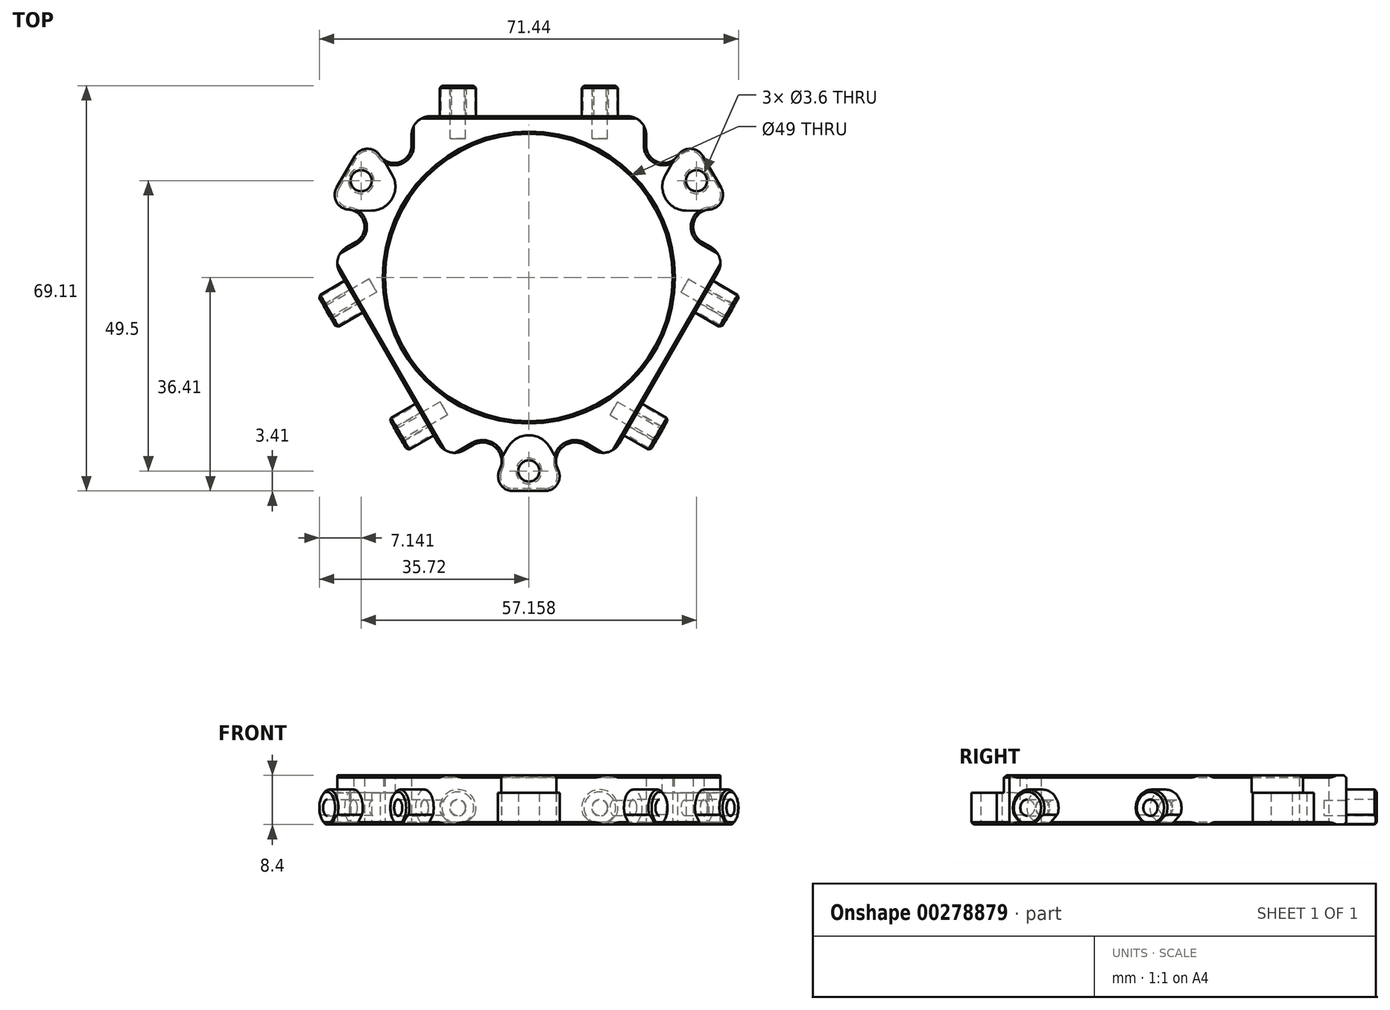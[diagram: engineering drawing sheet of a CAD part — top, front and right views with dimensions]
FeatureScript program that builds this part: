
annotation { "Feature Type Name" : "Feature", "Feature Type Description" : "" }
export const myFeature = defineFeature(function(context is Context, id is Id, definition is map)
    precondition{}
    {
        {
            var Q0;
            Q0=qCreatedBy(makeId("Top.planeOp"),FACE);
            var sketch = newSketch(context, id + "F0", { "sketchPlane" : qUnion([Q0])});
            skArc(sketch, "E0", {"start": v(3.94, -31.71) * mm, "mid": v(0, -27) * mm, "end": v(-3.94, -31.71) * mm});
            skArc(sketch, "E1", {"start": v(0.48, -34.97) * mm, "mid": v(4.46, -35.73) * mm, "end": v(3.94, -31.71) * mm});
            skLineSegment(sketch, "E2", {"start": v(3.73, -29.55) * mm, "end": v(5.07, -33) * mm});
            skCircle(sketch, "E3", {"center": v(0, 0) * mm, "radius": 24.5 * mm});
            skLineSegment(sketch, "E4", {"start": v(2.75, -36.4) * mm, "end": v(0, -36.4) * mm});
            skLineSegment(sketch, "E5.MirrorCS", {"start": v(-3.73, -29.55) * mm, "end": v(-5.07, -33) * mm});
            skArc(sketch, "E6.MirrorCS", {"start": v(-0.48, -34.97) * mm, "mid": v(-4.46, -35.73) * mm, "end": v(-3.94, -31.71) * mm});
            skLineSegment(sketch, "E7.MirrorCS", {"start": v(-2.75, -36.4) * mm, "end": v(0, -36.4) * mm});
            skLineSegment(sketch, "E8", {"start": v(0, 27.5) * mm, "end": v(12, 27.5) * mm});
            skLineSegment(sketch, "E9", {"start": v(12, 27.5) * mm, "end": v(20, 27.5) * mm});
            skLineSegment(sketch, "E10", {"start": v(20, 27.5) * mm, "end": v(20, 22.5) * mm});
            skLineSegment(sketch, "E11.MirrorCS", {"start": v(0, 27.5) * mm, "end": v(-12, 27.5) * mm});
            skLineSegment(sketch, "E12.MirrorCS", {"start": v(-12, 27.5) * mm, "end": v(-20, 27.5) * mm});
            skLineSegment(sketch, "E13.MirrorCS", {"start": v(-20, 27.5) * mm, "end": v(-20, 22.5) * mm});
            skLineSegment(sketch, "E14.1.0", {"start": v(-13.82, -31.07) * mm, "end": v(-9.49, -28.57) * mm});
            skLineSegment(sketch, "E14.1.1", {"start": v(-17.82, -24.14) * mm, "end": v(-13.82, -31.07) * mm});
            skLineSegment(sketch, "E14.1.2", {"start": v(-23.82, -13.75) * mm, "end": v(-17.82, -24.14) * mm});
            skLineSegment(sketch, "E14.1.3", {"start": v(-23.82, -13.75) * mm, "end": v(-29.82, -3.36) * mm});
            skLineSegment(sketch, "E14.1.4", {"start": v(-29.82, -3.36) * mm, "end": v(-33.82, 3.57) * mm});
            skLineSegment(sketch, "E14.1.5", {"start": v(-33.82, 3.57) * mm, "end": v(-29.49, 6.07) * mm});
            skLineSegment(sketch, "E14.2.0", {"start": v(33.82, 3.57) * mm, "end": v(29.49, 6.07) * mm});
            skLineSegment(sketch, "E14.2.1", {"start": v(29.82, -3.36) * mm, "end": v(33.82, 3.57) * mm});
            skLineSegment(sketch, "E14.2.2", {"start": v(23.82, -13.75) * mm, "end": v(29.82, -3.36) * mm});
            skLineSegment(sketch, "E14.2.3", {"start": v(23.82, -13.75) * mm, "end": v(17.82, -24.14) * mm});
            skLineSegment(sketch, "E14.2.4", {"start": v(17.82, -24.14) * mm, "end": v(13.82, -31.07) * mm});
            skLineSegment(sketch, "E14.2.5", {"start": v(13.82, -31.07) * mm, "end": v(9.49, -28.57) * mm});
            skArc(sketch, "E15", {"start": v(9.49, -28.57) * mm, "mid": v(5.58, -29.09) * mm, "end": v(5.07, -33) * mm});
            skArc(sketch, "E16.MirrorCS", {"start": v(-9.49, -28.57) * mm, "mid": v(-5.58, -29.09) * mm, "end": v(-5.07, -33) * mm});
            skArc(sketch, "E17.trimOffspring", {"start": v(-0.48, -34.97) * mm, "mid": v(0, -35) * mm, "end": v(0.48, -34.97) * mm});
            skArc(sketch, "E18.1.1", {"start": v(25.02, 19.06) * mm, "mid": v(23.38, 13.5) * mm, "end": v(29.01, 12.14) * mm});
            skArc(sketch, "E18.1.2", {"start": v(29.7, 18.3) * mm, "mid": v(27.9, 21.92) * mm, "end": v(25.02, 19.06) * mm});
            skArc(sketch, "E18.1.3", {"start": v(30.7, 16.58) * mm, "mid": v(32.92, 13.2) * mm, "end": v(29.01, 12.14) * mm});
            skArc(sketch, "E18.1.4", {"start": v(30.7, 16.58) * mm, "mid": v(30.31, 17.5) * mm, "end": v(29.7, 18.3) * mm});
            skLineSegment(sketch, "E18.1.5", {"start": v(26.94, 11.5) * mm, "end": v(30.64, 11.58) * mm});
            skLineSegment(sketch, "E18.1.6", {"start": v(23.43, 17.58) * mm, "end": v(25.35, 20.75) * mm});
            skLineSegment(sketch, "E18.1.7", {"start": v(29.65, 20.7) * mm, "end": v(31.2, 18.02) * mm});
            skLineSegment(sketch, "E18.1.8", {"start": v(32.75, 15.33) * mm, "end": v(31.2, 18.02) * mm});
            skArc(sketch, "E18.1.9", {"start": v(20, 22.5) * mm, "mid": v(22.04, 19.68) * mm, "end": v(25.35, 20.75) * mm});
            skArc(sketch, "E18.1.10", {"start": v(29.49, 6.07) * mm, "mid": v(28.07, 9.25) * mm, "end": v(30.64, 11.58) * mm});
            skArc(sketch, "E18.2.1", {"start": v(-29.01, 12.14) * mm, "mid": v(-23.38, 13.5) * mm, "end": v(-25.02, 19.06) * mm});
            skArc(sketch, "E18.2.2", {"start": v(-30.7, 16.58) * mm, "mid": v(-32.92, 13.2) * mm, "end": v(-29.01, 12.14) * mm});
            skArc(sketch, "E18.2.3", {"start": v(-29.7, 18.3) * mm, "mid": v(-27.9, 21.92) * mm, "end": v(-25.02, 19.06) * mm});
            skArc(sketch, "E18.2.4", {"start": v(-29.7, 18.3) * mm, "mid": v(-30.31, 17.5) * mm, "end": v(-30.7, 16.58) * mm});
            skLineSegment(sketch, "E18.2.5", {"start": v(-23.43, 17.58) * mm, "end": v(-25.35, 20.75) * mm});
            skLineSegment(sketch, "E18.2.6", {"start": v(-26.94, 11.5) * mm, "end": v(-30.64, 11.58) * mm});
            skLineSegment(sketch, "E18.2.7", {"start": v(-32.75, 15.33) * mm, "end": v(-31.2, 18.02) * mm});
            skLineSegment(sketch, "E18.2.8", {"start": v(-29.65, 20.7) * mm, "end": v(-31.2, 18.02) * mm});
            skArc(sketch, "E18.2.9", {"start": v(-29.49, 6.07) * mm, "mid": v(-28.07, 9.25) * mm, "end": v(-30.64, 11.58) * mm});
            skArc(sketch, "E18.2.10", {"start": v(-20, 22.5) * mm, "mid": v(-22.04, 19.68) * mm, "end": v(-25.35, 20.75) * mm});
            skCircle(sketch, "E19", {"center": v(0, -33) * mm, "radius": 1.8 * mm});
            skCircle(sketch, "E20.1.0", {"center": v(28.58, 16.5) * mm, "radius": 1.8 * mm});
            skCircle(sketch, "E20.2.0", {"center": v(-28.58, 16.5) * mm, "radius": 1.8 * mm});
            skSolve(sketch);
        }
        {
            var Q0;
            Q0=qSketchRegion(id+"F0",true);
            extrude(context, id + "F1", {"entities" : qUnion([Q0]), "depth" : 8.4 * mm, "offsetDistance" : 25 * mm});
        }
        {
            var Q0;
            Q0=makeQuery(id+"F1.opExtrude","SWEPT_FACE",FACE,{"disambiguationData":[OSD([sQuery(id+"F0.wireOp",EDGE,"E8"),sQuery(id+"F0.wireOp",EDGE,"E9"),sQuery(id+"F0.wireOp",EDGE,"E11.MirrorCS"),sQuery(id+"F0.wireOp",EDGE,"E12.MirrorCS")])]});
            var sketch = newSketch(context, id + "F2", { "sketchPlane" : qUnion([Q0])});
            skCircle(sketch, "E21.cCircle", {"center": v(-12.1, 2.86) * mm, "radius": 2.86 * mm, "construction": true});
            skLineSegment(sketch, "E21.0", {"start": v(-13.29, 5.73) * mm, "end": v(-10.91, 5.73) * mm});
            skLineSegment(sketch, "E21.1", {"start": v(-10.91, 5.73) * mm, "end": v(-9.24, 4.05) * mm});
            skLineSegment(sketch, "E21.2", {"start": v(-9.24, 4.05) * mm, "end": v(-9.24, 1.68) * mm});
            skLineSegment(sketch, "E21.3", {"start": v(-9.24, 1.68) * mm, "end": v(-10.91, 0) * mm});
            skLineSegment(sketch, "E21.4", {"start": v(-10.91, 0) * mm, "end": v(-13.29, 0) * mm});
            skLineSegment(sketch, "E21.5", {"start": v(-13.29, 0) * mm, "end": v(-14.96, 1.68) * mm});
            skLineSegment(sketch, "E21.6", {"start": v(-14.96, 1.68) * mm, "end": v(-14.96, 4.05) * mm});
            skLineSegment(sketch, "E21.7", {"start": v(-14.96, 4.05) * mm, "end": v(-13.29, 5.73) * mm});
            skPoint(sketch, "E21.0.midPoint", {"position": v(-12.1, 5.73) * mm});
            skArc(sketch, "E22", {"start": v(-9.24, 1.68) * mm, "mid": v(-12.1, 5.96) * mm, "end": v(-14.96, 1.68) * mm});
            skLineSegment(sketch, "E23.MirrorCS", {"start": v(10.91, 5.73) * mm, "end": v(9.24, 4.05) * mm});
            skLineSegment(sketch, "E24.MirrorCS", {"start": v(9.24, 4.05) * mm, "end": v(9.24, 1.68) * mm});
            skLineSegment(sketch, "E25.MirrorCS", {"start": v(14.96, 1.68) * mm, "end": v(14.96, 4.05) * mm});
            skLineSegment(sketch, "E26.MirrorCS", {"start": v(9.24, 1.68) * mm, "end": v(10.91, 0) * mm});
            skLineSegment(sketch, "E27.MirrorCS", {"start": v(14.96, 4.05) * mm, "end": v(13.29, 5.73) * mm});
            skLineSegment(sketch, "E28.MirrorCS", {"start": v(13.29, 5.73) * mm, "end": v(10.91, 5.73) * mm});
            skLineSegment(sketch, "E29.MirrorCS", {"start": v(10.91, 0) * mm, "end": v(13.29, 0) * mm});
            skLineSegment(sketch, "E30.MirrorCS", {"start": v(13.29, 0) * mm, "end": v(14.96, 1.68) * mm});
            skArc(sketch, "E31.MirrorCS", {"start": v(9.24, 1.68) * mm, "mid": v(12.1, 5.96) * mm, "end": v(14.96, 1.68) * mm});
            skPoint(sketch, "E32.MirrorP", {"position": v(12.1, 5.73) * mm});
            skCircle(sketch, "E33.MirrorC", {"center": v(12.1, 2.86) * mm, "radius": 2.86 * mm, "construction": true});
            skCircle(sketch, "E34", {"center": v(-12.1, 2.86) * mm, "radius": 1.4 * mm});
            skCircle(sketch, "E35.MirrorC", {"center": v(12.1, 2.86) * mm, "radius": 1.4 * mm});
            skSolve(sketch);
        }
        {
            var Q0;
            Q0=qSketchRegion(id+"F2",true);
            extrude(context, id + "F3", {"entities" : qUnion([Q0]), "depth" : 5.2 * mm, "offsetDistance" : 25 * mm});
        }
        {
            var Q0;
            Q0=makeQuery(id+"F3.opExtrude","CAP_FACE",FACE,{"disambiguationData":[OSD([sQuery(id+"F2.wireOp",EDGE,"E21.3"),sQuery(id+"F2.wireOp",EDGE,"E21.4"),sQuery(id+"F2.wireOp",EDGE,"E21.5"),sQuery(id+"F2.wireOp",EDGE,"E22"),sQuery(id+"F2.wireOp",EDGE,"E34")])],"isStart":false});
            var sketch = newSketch(context, id + "F4", { "sketchPlane" : qUnion([Q0])});
            skSolve(sketch);
        }
        {
            var Q0;
            Q0=makeQuery(id+"F3.opExtrude","SWEPT_BODY",BODY,{"disambiguationData":[OSD([sQuery(id+"F2.wireOp",EDGE,"E21.0"),sQuery(id+"F2.wireOp",EDGE,"E21.1"),sQuery(id+"F2.wireOp",EDGE,"E21.2"),sQuery(id+"F2.wireOp",EDGE,"E21.3"),sQuery(id+"F2.wireOp",EDGE,"E21.4"),sQuery(id+"F2.wireOp",EDGE,"E21.5"),sQuery(id+"F2.wireOp",EDGE,"E21.6"),sQuery(id+"F2.wireOp",EDGE,"E21.7")])]});
            var Q1;
            Q1=makeQuery(id+"F3.opExtrude","SWEPT_BODY",BODY,{"disambiguationData":[OSD([sQuery(id+"F2.wireOp",EDGE,"E26.MirrorCS"),sQuery(id+"F2.wireOp",EDGE,"E29.MirrorCS"),sQuery(id+"F2.wireOp",EDGE,"E30.MirrorCS"),sQuery(id+"F2.wireOp",EDGE,"E31.MirrorCS")])]});
            var Q2;
            Q2=makeQuery(id+"F1.opExtrude","CAP_EDGE",EDGE,{"disambiguationData":[OSD([sQuery(id+"F0.wireOp",EDGE,"E3")])],"isStart":false});
            circularPattern(context, id + "F5", {"operationType" : NewBodyOperationType.ADD, "entities" : qUnion([Q0, Q1]), "axis" : qUnion([Q2]), "angle" : 360 * degree, "instanceCount" : 3, "equalSpace" : true});
        }
        {
            var Q0;
            Q0=makeQuery(id+"F3.opExtrude","CAP_FACE",FACE,{"disambiguationData":[OSD([sQuery(id+"F2.wireOp",EDGE,"E21.3"),sQuery(id+"F2.wireOp",EDGE,"E21.4"),sQuery(id+"F2.wireOp",EDGE,"E21.5"),sQuery(id+"F2.wireOp",EDGE,"E22")])],"isStart":false});
            var sketch = newSketch(context, id + "F6", { "sketchPlane" : qUnion([Q0])});
            skCircle(sketch, "E36", {"center": v(-12.1, 2.86) * mm, "radius": 1.3 * mm});
            skCircle(sketch, "E37.MirrorC", {"center": v(12.1, 2.86) * mm, "radius": 1.3 * mm});
            skSolve(sketch);
        }
        {
            var Q0;
            Q0=qSketchRegion(id+"F6",true);
            extrude(context, id + "F7", {"entities" : qUnion([Q0]), "oppositeDirection" : true, "depth" : 9 * mm, "offsetDistance" : 25 * mm});
        }
        {
            var Q0;
            Q0=makeQuery(id+"F7.opExtrude","SWEPT_BODY",BODY,{"disambiguationData":[OSD([sQuery(id+"F6.wireOp",EDGE,"E37.MirrorC")])]});
            var Q1;
            Q1=makeQuery(id+"F7.opExtrude","SWEPT_BODY",BODY,{"disambiguationData":[OSD([sQuery(id+"F6.wireOp",EDGE,"E36")])]});
            var Q2;
            Q2=makeQuery(id+"F1.opExtrude","CAP_EDGE",EDGE,{"disambiguationData":[OSD([sQuery(id+"F0.wireOp",EDGE,"E3")])],"isStart":false});
            circularPattern(context, id + "F8", {"operationType" : NewBodyOperationType.REMOVE, "entities" : qUnion([Q0, Q1]), "axis" : qUnion([Q2]), "angle" : 360 * degree, "instanceCount" : 3, "equalSpace" : true});
        }
        {
            var Q0;
            {var subQ0=makeQuery(id+"F3.opExtrude","SWEPT_FACE",FACE,{"disambiguationData":[OSD([sQuery(id+"F2.wireOp",EDGE,"E29.MirrorCS")])]});var subQ1=makeQuery(id+"F3.opExtrude","SWEPT_FACE",FACE,{"disambiguationData":[OSD([sQuery(id+"F2.wireOp",EDGE,"E21.4")])]});Q0=makeQuery(id+"F5.boolean.opBoolean","MERGE",FACE,{"derivedFrom":[makeQuery(id+"F1.opExtrude","CAP_FACE",FACE,{"disambiguationData":[OSD([sQuery(id+"F0.wireOp",EDGE,"SqP7JoLz-BD9A-RXmz-Zu1V-RbqKSFD4Gl63"),sQuery(id+"F0.wireOp",EDGE,"Ud9Chbpr-zYe2-2spb-ifSY-rzAQWNdjOQxf"),sQuery(id+"F0.wireOp",EDGE,"bF6wv58Z-VzMq-CWjE-Sgwb-4WXWosELiao8"),sQuery(id+"F0.wireOp",EDGE,"cTkBJLnt-Smek-8MJw-4hbo-giizK2urv45t"),sQuery(id+"F0.wireOp",EDGE,"ae239fa6-1cef-4aa7-9151-0311c269b8940.MirrorCS"),sQuery(id+"F0.wireOp",EDGE,"ae239fa6-1cef-4aa7-9151-0311c269b8941.MirrorCS"),sQuery(id+"F0.wireOp",EDGE,"ae239fa6-1cef-4aa7-9151-0311c269b8943.MirrorCS"),sQuery(id+"F0.wireOp",EDGE,"ae239fa6-1cef-4aa7-9151-0311c269b8946.MirrorCS"),sQuery(id+"F0.wireOp",EDGE,"02da523c-332d-451a-b30c-e25d5381daab.1.0"),sQuery(id+"F0.wireOp",EDGE,"02da523c-332d-451a-b30c-e25d5381daab.1.1"),sQuery(id+"F0.wireOp",EDGE,"02da523c-332d-451a-b30c-e25d5381daab.1.2"),sQuery(id+"F0.wireOp",EDGE,"02da523c-332d-451a-b30c-e25d5381daab.1.5"),sQuery(id+"F0.wireOp",EDGE,"02da523c-332d-451a-b30c-e25d5381daab.1.6"),sQuery(id+"F0.wireOp",EDGE,"02da523c-332d-451a-b30c-e25d5381daab.1.8"),sQuery(id+"F0.wireOp",EDGE,"02da523c-332d-451a-b30c-e25d5381daab.1.9"),sQuery(id+"F0.wireOp",EDGE,"02da523c-332d-451a-b30c-e25d5381daab.1.15"),sQuery(id+"F0.wireOp",EDGE,"02da523c-332d-451a-b30c-e25d5381daab.1.16"),sQuery(id+"F0.wireOp",EDGE,"02da523c-332d-451a-b30c-e25d5381daab.2.0"),sQuery(id+"F0.wireOp",EDGE,"02da523c-332d-451a-b30c-e25d5381daab.2.1"),sQuery(id+"F0.wireOp",EDGE,"02da523c-332d-451a-b30c-e25d5381daab.2.2"),sQuery(id+"F0.wireOp",EDGE,"02da523c-332d-451a-b30c-e25d5381daab.2.5"),sQuery(id+"F0.wireOp",EDGE,"02da523c-332d-451a-b30c-e25d5381daab.2.6"),sQuery(id+"F0.wireOp",EDGE,"02da523c-332d-451a-b30c-e25d5381daab.2.8"),sQuery(id+"F0.wireOp",EDGE,"02da523c-332d-451a-b30c-e25d5381daab.2.9"),sQuery(id+"F0.wireOp",EDGE,"02da523c-332d-451a-b30c-e25d5381daab.2.11"),sQuery(id+"F0.wireOp",EDGE,"02da523c-332d-451a-b30c-e25d5381daab.2.15"),sQuery(id+"F0.wireOp",EDGE,"02da523c-332d-451a-b30c-e25d5381daab.2.16"),sQuery(id+"F0.wireOp",EDGE,"tuegAIGZ-9Pk6-ZTlW-QU7Y-IGKE2iZstJ9h"),sQuery(id+"F0.wireOp",EDGE,"fd02a02f-7cdf-416c-a631-e7393bf9c9300.MirrorC"),sQuery(id+"F0.wireOp",EDGE,"b5a6a487-fcb2-4526-9c33-14607ead2c7a.1.0"),sQuery(id+"F0.wireOp",EDGE,"b5a6a487-fcb2-4526-9c33-14607ead2c7a.1.1"),sQuery(id+"F0.wireOp",EDGE,"b5a6a487-fcb2-4526-9c33-14607ead2c7a.2.0"),sQuery(id+"F0.wireOp",EDGE,"b5a6a487-fcb2-4526-9c33-14607ead2c7a.2.1")])],"isStart":true}),subQ1,subQ0,makeQuery(id+"F5.opPattern","COPY",FACE,{"derivedFrom":subQ1,"instanceName":"1"}),makeQuery(id+"F5.opPattern","COPY",FACE,{"derivedFrom":subQ0,"instanceName":"1"}),makeQuery(id+"F5.opPattern","COPY",FACE,{"derivedFrom":subQ1,"instanceName":"2"}),makeQuery(id+"F5.opPattern","COPY",FACE,{"derivedFrom":subQ0,"instanceName":"2"})]});}
            var Q1;
            Q1=makeQuery(id+"F3.opExtrude","CAP_EDGE",EDGE,{"disambiguationData":[OSD([sQuery(id+"F2.wireOp",EDGE,"E31.MirrorCS")])],"isStart":false});
            var Q2;
            Q2=makeQuery(id+"F3.opExtrude","CAP_EDGE",EDGE,{"disambiguationData":[OSD([sQuery(id+"F2.wireOp",EDGE,"E22")])],"isStart":false});
            var Q3;
            Q3=makeQuery(id+"F5.opPattern","COPY",EDGE,{"derivedFrom":makeQuery(id+"F3.opExtrude","CAP_EDGE",EDGE,{"disambiguationData":[OSD([sQuery(id+"F2.wireOp",EDGE,"E31.MirrorCS")])],"isStart":false}),"instanceName":"2"});
            var Q4;
            Q4=makeQuery(id+"F5.opPattern","COPY",EDGE,{"derivedFrom":makeQuery(id+"F3.opExtrude","CAP_EDGE",EDGE,{"disambiguationData":[OSD([sQuery(id+"F2.wireOp",EDGE,"E22")])],"isStart":false}),"instanceName":"2"});
            var Q5;
            Q5=makeQuery(id+"F5.opPattern","COPY",EDGE,{"derivedFrom":makeQuery(id+"F3.opExtrude","CAP_EDGE",EDGE,{"disambiguationData":[OSD([sQuery(id+"F2.wireOp",EDGE,"E31.MirrorCS")])],"isStart":false}),"instanceName":"1"});
            var Q6;
            Q6=makeQuery(id+"F5.opPattern","COPY",EDGE,{"derivedFrom":makeQuery(id+"F3.opExtrude","CAP_EDGE",EDGE,{"disambiguationData":[OSD([sQuery(id+"F2.wireOp",EDGE,"E22")])],"isStart":false}),"instanceName":"1"});
            var Q7;
            Q7=makeQuery(id+"F1.opExtrude","CAP_FACE",FACE,{"disambiguationData":[OSD([sQuery(id+"F0.wireOp",EDGE,"SqP7JoLz-BD9A-RXmz-Zu1V-RbqKSFD4Gl63"),sQuery(id+"F0.wireOp",EDGE,"Ud9Chbpr-zYe2-2spb-ifSY-rzAQWNdjOQxf"),sQuery(id+"F0.wireOp",EDGE,"bF6wv58Z-VzMq-CWjE-Sgwb-4WXWosELiao8"),sQuery(id+"F0.wireOp",EDGE,"cTkBJLnt-Smek-8MJw-4hbo-giizK2urv45t"),sQuery(id+"F0.wireOp",EDGE,"ae239fa6-1cef-4aa7-9151-0311c269b8940.MirrorCS"),sQuery(id+"F0.wireOp",EDGE,"ae239fa6-1cef-4aa7-9151-0311c269b8941.MirrorCS"),sQuery(id+"F0.wireOp",EDGE,"ae239fa6-1cef-4aa7-9151-0311c269b8943.MirrorCS"),sQuery(id+"F0.wireOp",EDGE,"ae239fa6-1cef-4aa7-9151-0311c269b8946.MirrorCS"),sQuery(id+"F0.wireOp",EDGE,"02da523c-332d-451a-b30c-e25d5381daab.1.0"),sQuery(id+"F0.wireOp",EDGE,"02da523c-332d-451a-b30c-e25d5381daab.1.1"),sQuery(id+"F0.wireOp",EDGE,"02da523c-332d-451a-b30c-e25d5381daab.1.2"),sQuery(id+"F0.wireOp",EDGE,"02da523c-332d-451a-b30c-e25d5381daab.1.5"),sQuery(id+"F0.wireOp",EDGE,"02da523c-332d-451a-b30c-e25d5381daab.1.6"),sQuery(id+"F0.wireOp",EDGE,"02da523c-332d-451a-b30c-e25d5381daab.1.8"),sQuery(id+"F0.wireOp",EDGE,"02da523c-332d-451a-b30c-e25d5381daab.1.9"),sQuery(id+"F0.wireOp",EDGE,"02da523c-332d-451a-b30c-e25d5381daab.1.15"),sQuery(id+"F0.wireOp",EDGE,"02da523c-332d-451a-b30c-e25d5381daab.1.16"),sQuery(id+"F0.wireOp",EDGE,"02da523c-332d-451a-b30c-e25d5381daab.2.0"),sQuery(id+"F0.wireOp",EDGE,"02da523c-332d-451a-b30c-e25d5381daab.2.1"),sQuery(id+"F0.wireOp",EDGE,"02da523c-332d-451a-b30c-e25d5381daab.2.2"),sQuery(id+"F0.wireOp",EDGE,"02da523c-332d-451a-b30c-e25d5381daab.2.5"),sQuery(id+"F0.wireOp",EDGE,"02da523c-332d-451a-b30c-e25d5381daab.2.6"),sQuery(id+"F0.wireOp",EDGE,"02da523c-332d-451a-b30c-e25d5381daab.2.8"),sQuery(id+"F0.wireOp",EDGE,"02da523c-332d-451a-b30c-e25d5381daab.2.9"),sQuery(id+"F0.wireOp",EDGE,"02da523c-332d-451a-b30c-e25d5381daab.2.11"),sQuery(id+"F0.wireOp",EDGE,"02da523c-332d-451a-b30c-e25d5381daab.2.15"),sQuery(id+"F0.wireOp",EDGE,"02da523c-332d-451a-b30c-e25d5381daab.2.16"),sQuery(id+"F0.wireOp",EDGE,"tuegAIGZ-9Pk6-ZTlW-QU7Y-IGKE2iZstJ9h"),sQuery(id+"F0.wireOp",EDGE,"fd02a02f-7cdf-416c-a631-e7393bf9c9300.MirrorC"),sQuery(id+"F0.wireOp",EDGE,"b5a6a487-fcb2-4526-9c33-14607ead2c7a.1.0"),sQuery(id+"F0.wireOp",EDGE,"b5a6a487-fcb2-4526-9c33-14607ead2c7a.1.1"),sQuery(id+"F0.wireOp",EDGE,"b5a6a487-fcb2-4526-9c33-14607ead2c7a.2.0"),sQuery(id+"F0.wireOp",EDGE,"b5a6a487-fcb2-4526-9c33-14607ead2c7a.2.1")])],"isStart":false});
            var Q8;
            Q8=makeQuery(id+"F1.opExtrude","CAP_FACE",FACE,{"disambiguationData":[OSD([sQuery(id+"F0.wireOp",EDGE,"E1"),sQuery(id+"F0.wireOp",EDGE,"E3"),sQuery(id+"F0.wireOp",EDGE,"E4"),sQuery(id+"F0.wireOp",EDGE,"E6.MirrorCS"),sQuery(id+"F0.wireOp",EDGE,"E7.MirrorCS"),sQuery(id+"F0.wireOp",EDGE,"NR2aZ9zS-O8kZ-dOxt-Ha0G-w07LVY2dGel9"),sQuery(id+"F0.wireOp",EDGE,"E8"),sQuery(id+"F0.wireOp",EDGE,"E9"),sQuery(id+"F0.wireOp",EDGE,"E10"),sQuery(id+"F0.wireOp",EDGE,"E11.MirrorCS"),sQuery(id+"F0.wireOp",EDGE,"E12.MirrorCS"),sQuery(id+"F0.wireOp",EDGE,"E13.MirrorCS"),sQuery(id+"F0.wireOp",EDGE,"E14.1.0"),sQuery(id+"F0.wireOp",EDGE,"E14.1.1"),sQuery(id+"F0.wireOp",EDGE,"E14.1.2"),sQuery(id+"F0.wireOp",EDGE,"E14.1.3"),sQuery(id+"F0.wireOp",EDGE,"E14.1.4"),sQuery(id+"F0.wireOp",EDGE,"E14.1.5"),sQuery(id+"F0.wireOp",EDGE,"E14.2.0"),sQuery(id+"F0.wireOp",EDGE,"E14.2.1"),sQuery(id+"F0.wireOp",EDGE,"E14.2.2"),sQuery(id+"F0.wireOp",EDGE,"E14.2.3"),sQuery(id+"F0.wireOp",EDGE,"E14.2.4"),sQuery(id+"F0.wireOp",EDGE,"E14.2.5"),sQuery(id+"F0.wireOp",EDGE,"E15"),sQuery(id+"F0.wireOp",EDGE,"E16.MirrorCS"),sQuery(id+"F0.wireOp",EDGE,"E18.1.0"),sQuery(id+"F0.wireOp",EDGE,"E18.1.2"),sQuery(id+"F0.wireOp",EDGE,"E18.1.3"),sQuery(id+"F0.wireOp",EDGE,"E18.1.7"),sQuery(id+"F0.wireOp",EDGE,"E18.1.8"),sQuery(id+"F0.wireOp",EDGE,"E18.1.9"),sQuery(id+"F0.wireOp",EDGE,"E18.1.10"),sQuery(id+"F0.wireOp",EDGE,"E18.2.0"),sQuery(id+"F0.wireOp",EDGE,"E18.2.2"),sQuery(id+"F0.wireOp",EDGE,"E18.2.3"),sQuery(id+"F0.wireOp",EDGE,"E18.2.7"),sQuery(id+"F0.wireOp",EDGE,"E18.2.8"),sQuery(id+"F0.wireOp",EDGE,"E18.2.9"),sQuery(id+"F0.wireOp",EDGE,"E18.2.10")])],"isStart":false});
            chamfer(context, id + "F9", {"entities" : qUnion([Q0, Q1, Q2, Q3, Q4, Q5, Q6, Q7, Q8]), "width" : .4 * mm, "tangentPropagation" : true});
        }
        {
            var Q0;
            Q0=makeQuery(id+"F1.opExtrude","SWEPT_EDGE",EDGE,{"disambiguationData":[OSD([sQuery(id+"F0.wireOp",EDGE,"E14.1.4"),sQuery(id+"F0.wireOp",EDGE,"E14.1.5")])]});
            var Q1;
            Q1=makeQuery(id+"F1.opExtrude","SWEPT_EDGE",EDGE,{"disambiguationData":[OSD([sQuery(id+"F0.wireOp",EDGE,"E14.1.0"),sQuery(id+"F0.wireOp",EDGE,"E14.1.1")])]});
            var Q2;
            Q2=makeQuery(id+"F1.opExtrude","SWEPT_EDGE",EDGE,{"disambiguationData":[OSD([sQuery(id+"F0.wireOp",EDGE,"E14.2.4"),sQuery(id+"F0.wireOp",EDGE,"E14.2.5")])]});
            var Q3;
            Q3=makeQuery(id+"F1.opExtrude","SWEPT_EDGE",EDGE,{"disambiguationData":[OSD([sQuery(id+"F0.wireOp",EDGE,"E14.2.0"),sQuery(id+"F0.wireOp",EDGE,"E14.2.1")])]});
            var Q4;
            Q4=makeQuery(id+"F1.opExtrude","SWEPT_EDGE",EDGE,{"disambiguationData":[OSD([sQuery(id+"F0.wireOp",EDGE,"E9"),sQuery(id+"F0.wireOp",EDGE,"E10")])]});
            var Q5;
            Q5=makeQuery(id+"F1.opExtrude","SWEPT_EDGE",EDGE,{"disambiguationData":[OSD([sQuery(id+"F0.wireOp",EDGE,"E12.MirrorCS"),sQuery(id+"F0.wireOp",EDGE,"E13.MirrorCS")])]});
            fillet(context, id + "F10", {"entities" : qUnion([Q0, Q1, Q2, Q3, Q4, Q5]), "radius" : 3.2 * mm, "tangentPropagation" : true, "allowEdgeOverflow" : false});
        }
        {
            var Q0;
            Q0=makeQuery(id+"F1.opExtrude","CAP_FACE",FACE,{"disambiguationData":[OSD([sQuery(id+"F0.wireOp",EDGE,"E1"),sQuery(id+"F0.wireOp",EDGE,"E3"),sQuery(id+"F0.wireOp",EDGE,"E4"),sQuery(id+"F0.wireOp",EDGE,"E6.MirrorCS"),sQuery(id+"F0.wireOp",EDGE,"E7.MirrorCS"),sQuery(id+"F0.wireOp",EDGE,"NR2aZ9zS-O8kZ-dOxt-Ha0G-w07LVY2dGel9"),sQuery(id+"F0.wireOp",EDGE,"E8"),sQuery(id+"F0.wireOp",EDGE,"E9"),sQuery(id+"F0.wireOp",EDGE,"E10"),sQuery(id+"F0.wireOp",EDGE,"E11.MirrorCS"),sQuery(id+"F0.wireOp",EDGE,"E12.MirrorCS"),sQuery(id+"F0.wireOp",EDGE,"E13.MirrorCS"),sQuery(id+"F0.wireOp",EDGE,"E14.1.0"),sQuery(id+"F0.wireOp",EDGE,"E14.1.1"),sQuery(id+"F0.wireOp",EDGE,"E14.1.2"),sQuery(id+"F0.wireOp",EDGE,"E14.1.3"),sQuery(id+"F0.wireOp",EDGE,"E14.1.4"),sQuery(id+"F0.wireOp",EDGE,"E14.1.5"),sQuery(id+"F0.wireOp",EDGE,"E14.2.0"),sQuery(id+"F0.wireOp",EDGE,"E14.2.1"),sQuery(id+"F0.wireOp",EDGE,"E14.2.2"),sQuery(id+"F0.wireOp",EDGE,"E14.2.3"),sQuery(id+"F0.wireOp",EDGE,"E14.2.4"),sQuery(id+"F0.wireOp",EDGE,"E14.2.5"),sQuery(id+"F0.wireOp",EDGE,"E15"),sQuery(id+"F0.wireOp",EDGE,"E16.MirrorCS"),sQuery(id+"F0.wireOp",EDGE,"E18.1.0"),sQuery(id+"F0.wireOp",EDGE,"E18.1.2"),sQuery(id+"F0.wireOp",EDGE,"E18.1.3"),sQuery(id+"F0.wireOp",EDGE,"E18.1.7"),sQuery(id+"F0.wireOp",EDGE,"E18.1.8"),sQuery(id+"F0.wireOp",EDGE,"E18.1.9"),sQuery(id+"F0.wireOp",EDGE,"E18.1.10"),sQuery(id+"F0.wireOp",EDGE,"E18.2.0"),sQuery(id+"F0.wireOp",EDGE,"E18.2.2"),sQuery(id+"F0.wireOp",EDGE,"E18.2.3"),sQuery(id+"F0.wireOp",EDGE,"E18.2.7"),sQuery(id+"F0.wireOp",EDGE,"E18.2.8"),sQuery(id+"F0.wireOp",EDGE,"E18.2.9"),sQuery(id+"F0.wireOp",EDGE,"E18.2.10")])],"isStart":false});
            var sketch = newSketch(context, id + "F11", { "sketchPlane" : qUnion([Q0])});
            skArc(sketch, "E38", {"start": v(4.1, -31.08) * mm, "mid": v(0, -26.9) * mm, "end": v(-4.1, -31.08) * mm});
            skArc(sketch, "E39", {"start": v(0.22, -35.1) * mm, "mid": v(5.1, -35.94) * mm, "end": v(4.1, -31.08) * mm});
            skLineSegment(sketch, "E40", {"start": v(3.54, -28.93) * mm, "end": v(5.53, -32.33) * mm});
            skLineSegment(sketch, "E41", {"start": v(2.95, -36.85) * mm, "end": v(0, -36.85) * mm});
            skLineSegment(sketch, "E42.MirrorCS", {"start": v(-3.54, -28.93) * mm, "end": v(-5.53, -32.33) * mm});
            skArc(sketch, "E43.MirrorCS", {"start": v(-0.22, -35.1) * mm, "mid": v(-5.1, -35.94) * mm, "end": v(-4.1, -31.08) * mm});
            skLineSegment(sketch, "E44.MirrorCS", {"start": v(-2.95, -36.85) * mm, "end": v(0, -36.85) * mm});
            skArc(sketch, "E45.trimOffspring", {"start": v(-0.22, -35.1) * mm, "mid": v(0, -35.1) * mm, "end": v(0.22, -35.1) * mm});
            skPoint(sketch, "E46.center", {"position": v(0.1, -0.08) * mm});
            skArc(sketch, "E47.1.0", {"start": v(30.28, 17.74) * mm, "mid": v(28.57, 22.39) * mm, "end": v(24.87, 19.1) * mm});
            skLineSegment(sketch, "E47.1.1", {"start": v(30.44, 20.98) * mm, "end": v(31.91, 18.43) * mm});
            skLineSegment(sketch, "E47.1.2", {"start": v(33.39, 15.87) * mm, "end": v(31.91, 18.43) * mm});
            skArc(sketch, "E47.1.3", {"start": v(30.5, 17.36) * mm, "mid": v(33.67, 13.55) * mm, "end": v(28.97, 12) * mm});
            skArc(sketch, "E47.1.4", {"start": v(24.87, 19.1) * mm, "mid": v(23.3, 13.45) * mm, "end": v(28.97, 12) * mm});
            skLineSegment(sketch, "E47.1.5", {"start": v(26.82, 11.4) * mm, "end": v(30.77, 11.37) * mm});
            skLineSegment(sketch, "E47.1.6", {"start": v(23.28, 17.53) * mm, "end": v(25.23, 20.96) * mm});
            skArc(sketch, "E47.1.7", {"start": v(30.5, 17.36) * mm, "mid": v(30.4, 17.55) * mm, "end": v(30.28, 17.74) * mm});
            skArc(sketch, "E47.2.0", {"start": v(-30.5, 17.36) * mm, "mid": v(-33.67, 13.55) * mm, "end": v(-28.97, 12) * mm});
            skLineSegment(sketch, "E47.2.1", {"start": v(-33.39, 15.87) * mm, "end": v(-31.91, 18.43) * mm});
            skLineSegment(sketch, "E47.2.2", {"start": v(-30.44, 20.98) * mm, "end": v(-31.91, 18.43) * mm});
            skArc(sketch, "E47.2.3", {"start": v(-30.28, 17.74) * mm, "mid": v(-28.57, 22.39) * mm, "end": v(-24.87, 19.1) * mm});
            skArc(sketch, "E47.2.4", {"start": v(-28.97, 12) * mm, "mid": v(-23.3, 13.45) * mm, "end": v(-24.87, 19.1) * mm});
            skLineSegment(sketch, "E47.2.5", {"start": v(-23.28, 17.53) * mm, "end": v(-25.23, 20.96) * mm});
            skLineSegment(sketch, "E47.2.6", {"start": v(-26.82, 11.4) * mm, "end": v(-30.77, 11.37) * mm});
            skArc(sketch, "E47.2.7", {"start": v(-30.28, 17.74) * mm, "mid": v(-30.4, 17.55) * mm, "end": v(-30.5, 17.36) * mm});
            skPoint(sketch, "E47.center", {"position": v(0, 0) * mm});
            skSolve(sketch);
        }
        {
            var Q0;
            Q0 = qSketchRegion(id + "F11", true);
            extrude(context, id + "F12", {"entities" : qUnion([Q0]), "operationType" : NewBodyOperationType.REMOVE, "oppositeDirection" : true, "depth" : 3 * mm, "offsetDistance" : 25 * mm});
        }
    });
